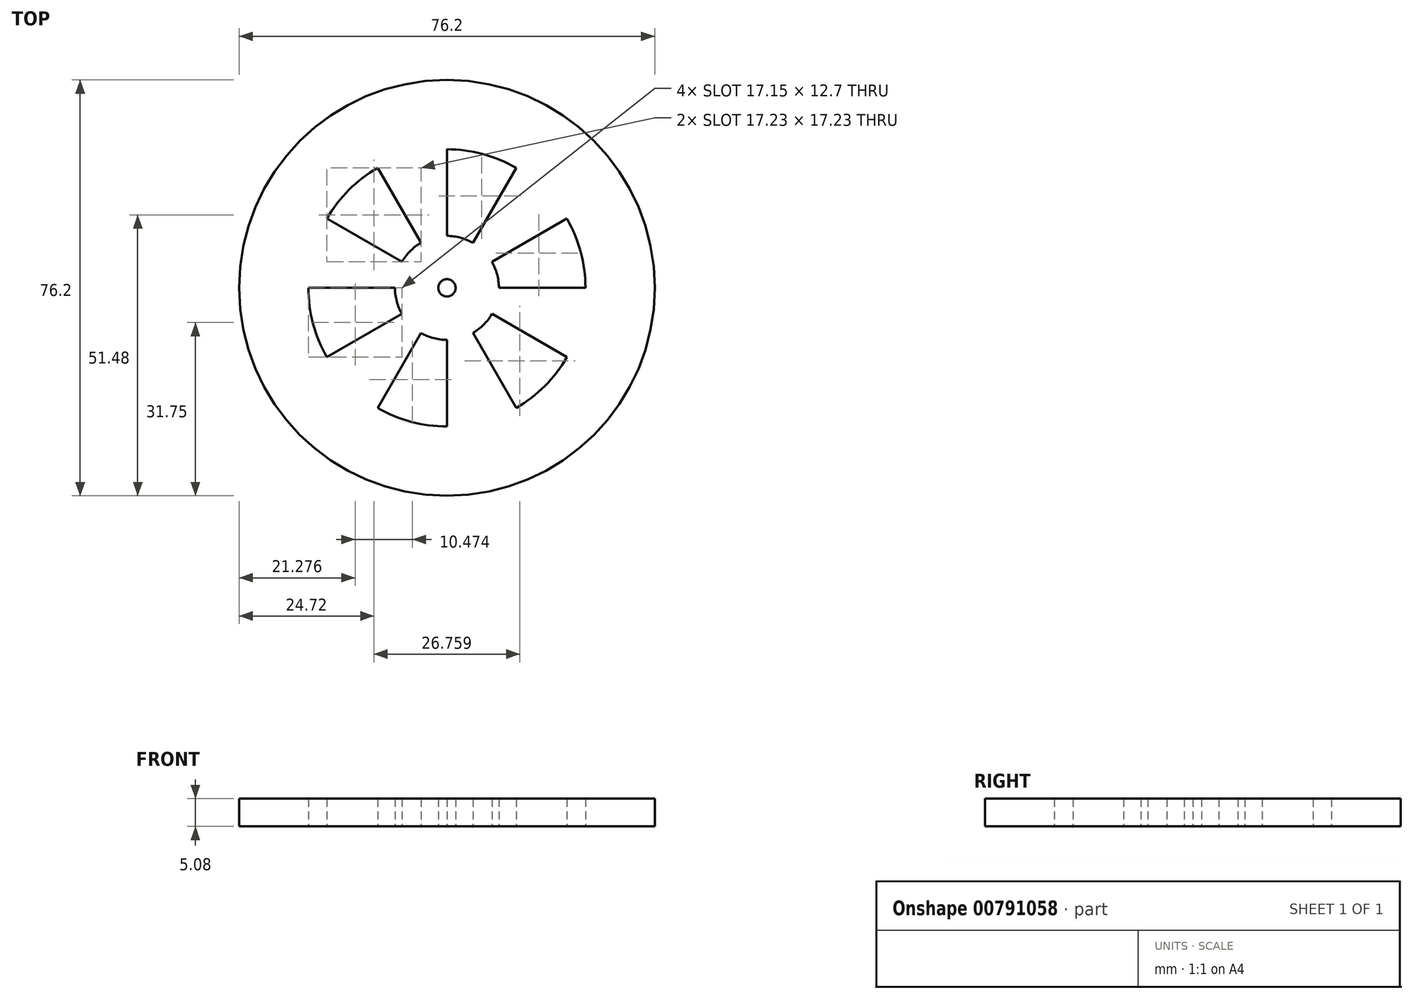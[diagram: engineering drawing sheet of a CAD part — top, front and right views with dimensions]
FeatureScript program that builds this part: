
annotation { "Feature Type Name" : "Feature", "Feature Type Description" : "" }
export const myFeature = defineFeature(function(context is Context, id is Id, definition is map)
    precondition{}
    {
        {
            var Q0;
            Q0=qCreatedBy(makeId("Top.planeOp"),FACE);
            var sketch = newSketch(context, id + "F0", { "sketchPlane" : qUnion([Q0])});
            skCircle(sketch, "E0", {"center": v(0, 0) * mm, "radius": 38.1 * mm});
            skCircle(sketch, "E1", {"center": v(0, 0) * mm, "radius": 25.4 * mm});
            skLineSegment(sketch, "E2", {"start": v(0, 0) * mm, "end": v(25.4, 0) * mm});
            skLineSegment(sketch, "E3", {"start": v(0, 0) * mm, "end": v(22, 12.7) * mm});
            skLineSegment(sketch, "E4", {"start": v(0, 0) * mm, "end": v(12.7, 22) * mm});
            skLineSegment(sketch, "E5", {"start": v(0, 0) * mm, "end": v(0, 25.4) * mm});
            skLineSegment(sketch, "E6", {"start": v(0, 0) * mm, "end": v(-12.7, 22) * mm});
            skLineSegment(sketch, "E7", {"start": v(0, 0) * mm, "end": v(-22, 12.7) * mm});
            skLineSegment(sketch, "E8", {"start": v(0, 0) * mm, "end": v(-25.4, 0) * mm});
            skLineSegment(sketch, "E9", {"start": v(0, 0) * mm, "end": v(-22, -12.7) * mm});
            skLineSegment(sketch, "E10", {"start": v(0, 0) * mm, "end": v(-12.7, -22) * mm});
            skLineSegment(sketch, "E11", {"start": v(0, 0) * mm, "end": v(0, -25.4) * mm});
            skLineSegment(sketch, "E12", {"start": v(0, 0) * mm, "end": v(12.7, -22) * mm});
            skLineSegment(sketch, "E13", {"start": v(0, 0) * mm, "end": v(22, -12.7) * mm});
            skCircle(sketch, "E14", {"center": v(0, 0) * mm, "radius": 9.53 * mm});
            skCircle(sketch, "E15", {"center": v(0, 0) * mm, "radius": 1.59 * mm});
            skSolve(sketch);
        }
        {
            var Q0;
            {var subQ0=sQuery(id+"F0.wireOp",EDGE,"E15");var subQ1=sQuery(id+"F0.wireOp",EDGE,"E9");var subQ2=makeQuery(id+"F0.imprint","INTERSECT",VERTEX,{"derivedFrom":[subQ1,subQ0]});Q0=makeQuery(id+"F0.imprint","IMPRINT",FACE,{"disambiguationData":[TD([[makeQuery(id+"F0.imprint","IMPRINT",EDGE,{"disambiguationData":[TD([[subQ2,-1.0]])],"derivedFrom":subQ1}),1.0]])]});}
            var Q1;
            {var subQ0=sQuery(id+"F0.wireOp",EDGE,"E15");var subQ1=sQuery(id+"F0.wireOp",EDGE,"E10");var subQ2=makeQuery(id+"F0.imprint","INTERSECT",VERTEX,{"derivedFrom":[subQ1,subQ0]});Q1=makeQuery(id+"F0.imprint","IMPRINT",FACE,{"disambiguationData":[TD([[makeQuery(id+"F0.imprint","IMPRINT",EDGE,{"disambiguationData":[TD([[subQ2,-1.0]])],"derivedFrom":subQ1}),1.0]])]});}
            var Q2;
            {var subQ0=sQuery(id+"F0.wireOp",EDGE,"E15");var subQ1=sQuery(id+"F0.wireOp",EDGE,"E11");var subQ2=makeQuery(id+"F0.imprint","INTERSECT",VERTEX,{"derivedFrom":[subQ1,subQ0]});Q2=makeQuery(id+"F0.imprint","IMPRINT",FACE,{"disambiguationData":[TD([[makeQuery(id+"F0.imprint","IMPRINT",EDGE,{"disambiguationData":[TD([[subQ2,-1.0]])],"derivedFrom":subQ1}),1.0]])]});}
            var Q3;
            {var subQ0=sQuery(id+"F0.wireOp",EDGE,"E15");var subQ1=sQuery(id+"F0.wireOp",EDGE,"E12");var subQ2=makeQuery(id+"F0.imprint","INTERSECT",VERTEX,{"derivedFrom":[subQ1,subQ0]});Q3=makeQuery(id+"F0.imprint","IMPRINT",FACE,{"disambiguationData":[TD([[makeQuery(id+"F0.imprint","IMPRINT",EDGE,{"disambiguationData":[TD([[subQ2,-1.0]])],"derivedFrom":subQ1}),1.0]])]});}
            var Q4;
            {var subQ0=sQuery(id+"F0.wireOp",EDGE,"E15");var subQ1=sQuery(id+"F0.wireOp",EDGE,"E2");var subQ2=makeQuery(id+"F0.imprint","INTERSECT",VERTEX,{"derivedFrom":[subQ1,subQ0]});Q4=makeQuery(id+"F0.imprint","IMPRINT",FACE,{"disambiguationData":[TD([[makeQuery(id+"F0.imprint","IMPRINT",EDGE,{"disambiguationData":[TD([[subQ2,-1.0]])],"derivedFrom":subQ1}),-1.0]])]});}
            var Q5;
            {var subQ0=sQuery(id+"F0.wireOp",EDGE,"E15");var subQ1=sQuery(id+"F0.wireOp",EDGE,"E2");var subQ2=makeQuery(id+"F0.imprint","INTERSECT",VERTEX,{"derivedFrom":[subQ1,subQ0]});Q5=makeQuery(id+"F0.imprint","IMPRINT",FACE,{"disambiguationData":[TD([[makeQuery(id+"F0.imprint","IMPRINT",EDGE,{"disambiguationData":[TD([[subQ2,-1.0]])],"derivedFrom":subQ1}),1.0]])]});}
            var Q6;
            {var subQ0=sQuery(id+"F0.wireOp",EDGE,"E15");var subQ1=sQuery(id+"F0.wireOp",EDGE,"E3");var subQ2=makeQuery(id+"F0.imprint","INTERSECT",VERTEX,{"derivedFrom":[subQ1,subQ0]});Q6=makeQuery(id+"F0.imprint","IMPRINT",FACE,{"disambiguationData":[TD([[makeQuery(id+"F0.imprint","IMPRINT",EDGE,{"disambiguationData":[TD([[subQ2,-1.0]])],"derivedFrom":subQ1}),1.0]])]});}
            var Q7;
            {var subQ0=sQuery(id+"F0.wireOp",EDGE,"E15");var subQ1=sQuery(id+"F0.wireOp",EDGE,"E4");var subQ2=makeQuery(id+"F0.imprint","INTERSECT",VERTEX,{"derivedFrom":[subQ1,subQ0]});Q7=makeQuery(id+"F0.imprint","IMPRINT",FACE,{"disambiguationData":[TD([[makeQuery(id+"F0.imprint","IMPRINT",EDGE,{"disambiguationData":[TD([[subQ2,-1.0]])],"derivedFrom":subQ1}),1.0]])]});}
            var Q8;
            {var subQ0=sQuery(id+"F0.wireOp",EDGE,"E15");var subQ1=sQuery(id+"F0.wireOp",EDGE,"E5");var subQ2=makeQuery(id+"F0.imprint","INTERSECT",VERTEX,{"derivedFrom":[subQ1,subQ0]});Q8=makeQuery(id+"F0.imprint","IMPRINT",FACE,{"disambiguationData":[TD([[makeQuery(id+"F0.imprint","IMPRINT",EDGE,{"disambiguationData":[TD([[subQ2,-1.0]])],"derivedFrom":subQ1}),1.0]])]});}
            var Q9;
            {var subQ0=sQuery(id+"F0.wireOp",EDGE,"E15");var subQ1=sQuery(id+"F0.wireOp",EDGE,"E6");var subQ2=makeQuery(id+"F0.imprint","INTERSECT",VERTEX,{"derivedFrom":[subQ1,subQ0]});Q9=makeQuery(id+"F0.imprint","IMPRINT",FACE,{"disambiguationData":[TD([[makeQuery(id+"F0.imprint","IMPRINT",EDGE,{"disambiguationData":[TD([[subQ2,-1.0]])],"derivedFrom":subQ1}),1.0]])]});}
            var Q10;
            {var subQ0=sQuery(id+"F0.wireOp",EDGE,"E15");var subQ1=sQuery(id+"F0.wireOp",EDGE,"E7");var subQ2=makeQuery(id+"F0.imprint","INTERSECT",VERTEX,{"derivedFrom":[subQ1,subQ0]});Q10=makeQuery(id+"F0.imprint","IMPRINT",FACE,{"disambiguationData":[TD([[makeQuery(id+"F0.imprint","IMPRINT",EDGE,{"disambiguationData":[TD([[subQ2,-1.0]])],"derivedFrom":subQ1}),1.0]])]});}
            var Q11;
            {var subQ0=sQuery(id+"F0.wireOp",EDGE,"E15");var subQ1=sQuery(id+"F0.wireOp",EDGE,"E8");var subQ2=makeQuery(id+"F0.imprint","INTERSECT",VERTEX,{"derivedFrom":[subQ1,subQ0]});Q11=makeQuery(id+"F0.imprint","IMPRINT",FACE,{"disambiguationData":[TD([[makeQuery(id+"F0.imprint","IMPRINT",EDGE,{"disambiguationData":[TD([[subQ2,-1.0]])],"derivedFrom":subQ1}),1.0]])]});}
            var Q12;
            {var subQ0=sQuery(id+"F0.wireOp",EDGE,"E3");var subQ1=sQuery(id+"F0.wireOp",EDGE,"E1");var subQ2=makeQuery(id+"F0.imprint","INTERSECT",VERTEX,{"derivedFrom":[subQ1,subQ0]});Q12=makeQuery(id+"F0.imprint","IMPRINT",FACE,{"disambiguationData":[TD([[makeQuery(id+"F0.imprint","IMPRINT",EDGE,{"disambiguationData":[TD([[subQ2,-1.0]])],"derivedFrom":subQ1}),1.0]])]});}
            var Q13;
            {var subQ0=sQuery(id+"F0.wireOp",EDGE,"E7");var subQ1=sQuery(id+"F0.wireOp",EDGE,"E1");var subQ2=makeQuery(id+"F0.imprint","INTERSECT",VERTEX,{"derivedFrom":[subQ1,subQ0]});Q13=makeQuery(id+"F0.imprint","IMPRINT",FACE,{"disambiguationData":[TD([[makeQuery(id+"F0.imprint","IMPRINT",EDGE,{"disambiguationData":[TD([[subQ2,-1.0]])],"derivedFrom":subQ1}),1.0]])]});}
            var Q14;
            {var subQ0=sQuery(id+"F0.wireOp",EDGE,"E9");var subQ1=sQuery(id+"F0.wireOp",EDGE,"E1");var subQ2=makeQuery(id+"F0.imprint","INTERSECT",VERTEX,{"derivedFrom":[subQ1,subQ0]});Q14=makeQuery(id+"F0.imprint","IMPRINT",FACE,{"disambiguationData":[TD([[makeQuery(id+"F0.imprint","IMPRINT",EDGE,{"disambiguationData":[TD([[subQ2,-1.0]])],"derivedFrom":subQ1}),1.0]])]});}
            var Q15;
            {var subQ0=sQuery(id+"F0.wireOp",EDGE,"E5");var subQ1=sQuery(id+"F0.wireOp",EDGE,"E1");var subQ2=makeQuery(id+"F0.imprint","INTERSECT",VERTEX,{"derivedFrom":[subQ1,subQ0]});Q15=makeQuery(id+"F0.imprint","IMPRINT",FACE,{"disambiguationData":[TD([[makeQuery(id+"F0.imprint","IMPRINT",EDGE,{"disambiguationData":[TD([[subQ2,-1.0]])],"derivedFrom":subQ1}),1.0]])]});}
            var Q16;
            {var subQ0=sQuery(id+"F0.wireOp",EDGE,"E11");var subQ1=sQuery(id+"F0.wireOp",EDGE,"E1");var subQ2=makeQuery(id+"F0.imprint","INTERSECT",VERTEX,{"derivedFrom":[subQ1,subQ0]});Q16=makeQuery(id+"F0.imprint","IMPRINT",FACE,{"disambiguationData":[TD([[makeQuery(id+"F0.imprint","IMPRINT",EDGE,{"disambiguationData":[TD([[subQ2,-1.0]])],"derivedFrom":subQ1}),1.0]])]});}
            var Q17;
            {var subQ0=sQuery(id+"F0.wireOp",EDGE,"E2");var subQ1=sQuery(id+"F0.wireOp",EDGE,"E1");var subQ2=makeQuery(id+"F0.imprint","INTERSECT",VERTEX,{"derivedFrom":[subQ1,subQ0]});Q17=makeQuery(id+"F0.imprint","IMPRINT",FACE,{"disambiguationData":[TD([[makeQuery(id+"F0.imprint","IMPRINT",EDGE,{"disambiguationData":[TD([[subQ2,1.0]])],"derivedFrom":subQ1}),1.0]])]});}
            var Q18;
            Q18=makeQuery(id+"F0.imprint","IMPRINT",FACE,{"disambiguationData":[TD([[makeQuery(id+"F0.imprint","IMPRINT",EDGE,{"derivedFrom":sQuery(id+"F0.wireOp",EDGE,"E0")}),1.0]])]});
            extrude(context, id + "F1", {"entities" : qUnion([Q0, Q1, Q2, Q3, Q4, Q5, Q6, Q7, Q8, Q9, Q10, Q11, Q12, Q13, Q14, Q15, Q16, Q17, Q18]), "depth" : 5.08 * mm, "offsetDistance" : 25.4 * mm});
        }
    });
